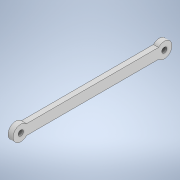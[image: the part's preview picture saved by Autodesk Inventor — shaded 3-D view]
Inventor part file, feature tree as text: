
AUTODESK INVENTOR PART (.ipt)
format: ipt  version: 2020 (Build 240168000, 168)  size: 111,616 bytes
history: native  units: in
note: dims shown in document units (in); Inventor stores cm internally (conversion verified against a paired STEP export)
features: sketch x2, extrude x1, hole x1, mirror x1, projected_geometry x1
ambient origin geometry x8: Origin, YZ Plane, XZ Plane, XY Plane, X Axis, Y Axis, Z Axis, Center Point
bodies: Solid1 (feature_tree)
feature tree (6):
  extrude  "Extrusion1"  Depth=0.125in TaperAngle=0.0deg
  hole  "Hole1"  [1 undecoded]
  mirror  "Mirror1"
  sketch  "Sketch1"  dims[d0=0.25in d3=0.125in d4=0.0in]
  sketch  "Sketch2"  dims[d5=0.128in d6=0.5in d7=0.375in d8=0.25in d9=0.5635in d10=1.0in d11=0.8108in]
  projected_geometry  "Projected Loop1"
note: 1 required parameter value undecoded (feature->parameter linkage not recoverable at this tier; creation-order binding heuristic only, values carry confidence <= 0.55)
